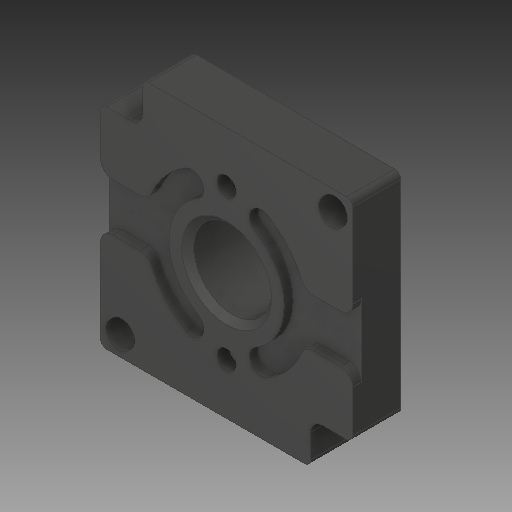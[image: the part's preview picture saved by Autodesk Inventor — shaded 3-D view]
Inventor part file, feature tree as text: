
AUTODESK INVENTOR PART (.ipt)
format: ipt  version: 2017 (Build 210142000, 142)  size: 323,584 bytes
history: native  units: in
note: dims shown in document units (in); Inventor stores cm internally (conversion verified against a paired STEP export)
features: fillet x1
ambient origin geometry x8: Origin, YZ Plane, XZ Plane, XY Plane, X Axis, Y Axis, Z Axis, Center Point
bodies: Solid1 (feature_tree)
feature tree (1):
  fillet  "Fillet4"  [1 undecoded]
note: 1 required parameter value undecoded (feature->parameter linkage not recoverable at this tier; creation-order binding heuristic only, values carry confidence <= 0.55)
